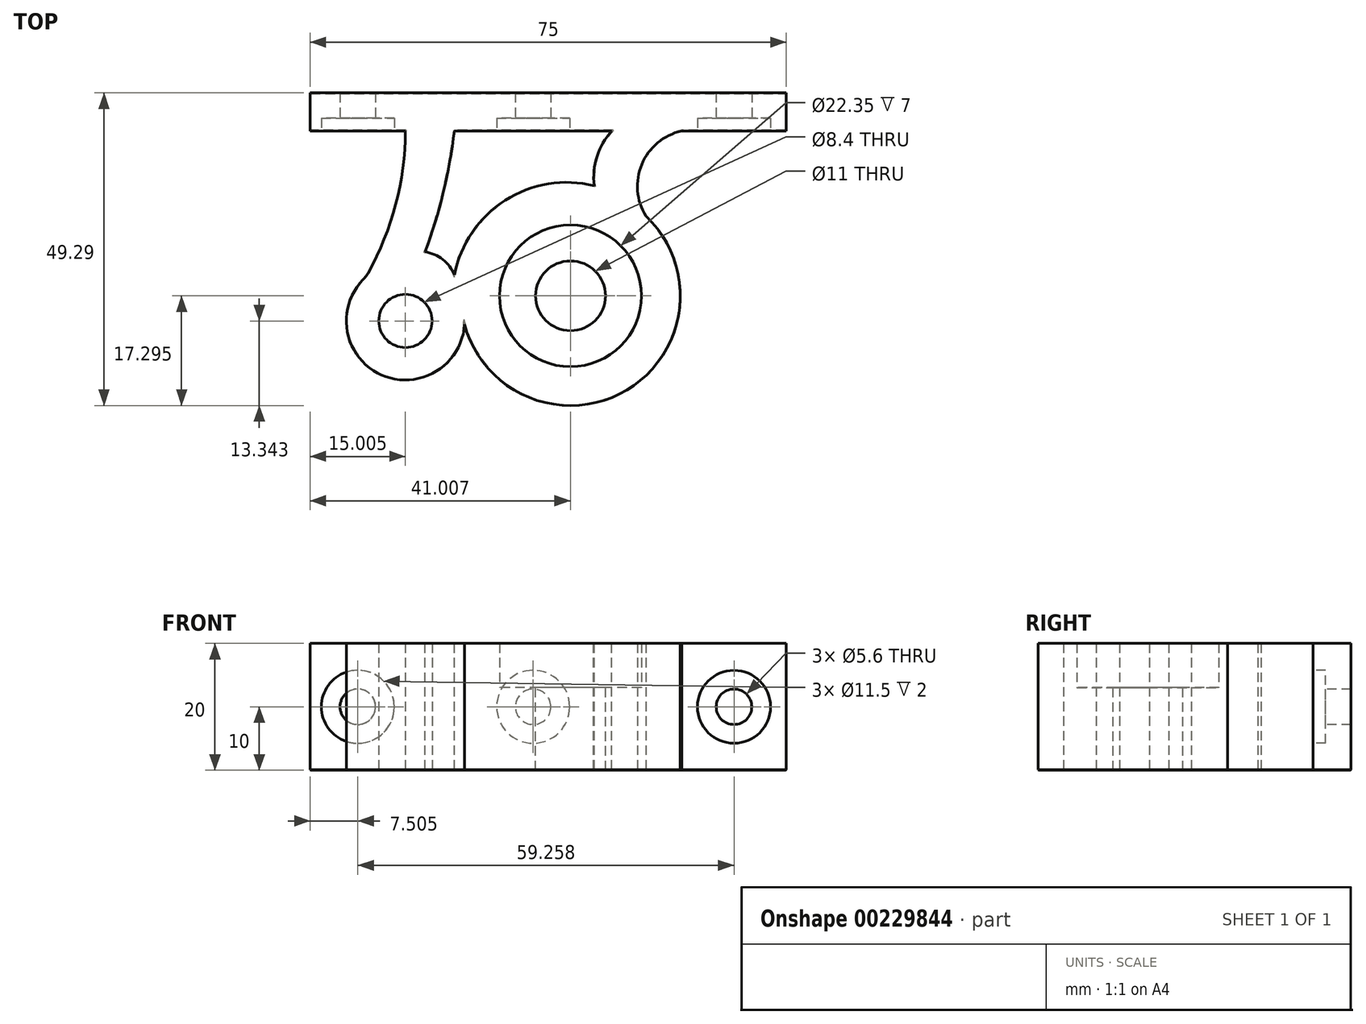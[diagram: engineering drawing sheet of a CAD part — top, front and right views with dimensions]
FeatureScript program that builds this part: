
annotation { "Feature Type Name" : "Feature", "Feature Type Description" : "" }
export const myFeature = defineFeature(function(context is Context, id is Id, definition is map)
    precondition{}
    {
        {
            var Q0;
            Q0=qCreatedBy(makeId("Top.planeOp"),FACE);
            var sketch = newSketch(context, id + "F0", { "sketchPlane" : qUnion([Q0])});
            skCircle(sketch, "E0", {"center": v(-26.48, -0.93) * mm, "radius": 4.2 * mm});
            skLineSegment(sketch, "E1", {"start": v(-26.48, -0.93) * mm, "end": v(-0.47, -0.93) * mm, "construction": true});
            skLineSegment(sketch, "E2", {"start": v(-0.47, -0.93) * mm, "end": v(-0.47, 3.02) * mm, "construction": true});
            skLineSegment(sketch, "E3", {"start": v(-26.48, -0.93) * mm, "end": v(-26.48, 35.02) * mm, "construction": true});
            skCircle(sketch, "E4", {"center": v(-0.47, 3.02) * mm, "radius": 11.18 * mm});
            skLineSegment(sketch, "E5", {"start": v(-26.48, 35.02) * mm, "end": v(-41.48, 35.02) * mm});
            skLineSegment(sketch, "E6", {"start": v(-41.48, 35.02) * mm, "end": v(-41.48, 29.02) * mm});
            skLineSegment(sketch, "E7", {"start": v(-26.48, 35.02) * mm, "end": v(33.52, 35.02) * mm});
            skLineSegment(sketch, "E8", {"start": v(33.52, 35.02) * mm, "end": v(33.52, 29.02) * mm});
            skLineSegment(sketch, "E9", {"start": v(17.04, 29.02) * mm, "end": v(33.52, 29.02) * mm});
            skLineSegment(sketch, "E10", {"start": v(-41.48, 29.02) * mm, "end": v(-26.48, 29.02) * mm});
            skArc(sketch, "E11", {"start": v(-32.73, 5.97) * mm, "mid": v(-30.5, -9.33) * mm, "end": v(-17.17, -1.48) * mm});
            skArc(sketch, "E12", {"start": v(-32.73, 5.97) * mm, "mid": v(-28.1, 17.09) * mm, "end": v(-26.48, 29.02) * mm});
            skArc(sketch, "E13", {"start": v(-17.17, -1.48) * mm, "mid": v(8.4, -11.83) * mm, "end": v(11.41, 15.6) * mm});
            skArc(sketch, "E14", {"start": v(17.04, 29.02) * mm, "mid": v(10.76, 23.76) * mm, "end": v(11.41, 15.6) * mm});
            skSolve(sketch);
        }
        {
            var Q0;
            Q0=makeQuery(id+"F0.imprint","IMPRINT",FACE,{"disambiguationData":[TD([[makeQuery(id+"F0.imprint","IMPRINT",EDGE,{"derivedFrom":sQuery(id+"F0.wireOp",EDGE,"E0")}),-1.0]])]});
            extrude(context, id + "F1", {"entities" : qUnion([Q0]), "depth" : 20 * mm});
        }
        {
            var Q0;
            Q0=makeQuery(id+"F1.opExtrude","CAP_FACE",FACE,{"disambiguationData":[OSD([sQuery(id+"F0.wireOp",EDGE,"E0"),sQuery(id+"F0.wireOp",EDGE,"E4"),sQuery(id+"F0.wireOp",EDGE,"E5"),sQuery(id+"F0.wireOp",EDGE,"E6"),sQuery(id+"F0.wireOp",EDGE,"E7"),sQuery(id+"F0.wireOp",EDGE,"E8"),sQuery(id+"F0.wireOp",EDGE,"rnpyxZyI-oq2V-pBoN-Qr8R-ykEtNN3jd1BS"),sQuery(id+"F0.wireOp",EDGE,"xY3NNHAz-ocZd-zQ1a-BtMq-btxev2WQv32X"),sQuery(id+"F0.wireOp",EDGE,"IQkoVCXJ-aQl7-kOCh-NkcK-sWtL1LuhfyMV"),sQuery(id+"F0.wireOp",EDGE,"E9"),sQuery(id+"F0.wireOp",EDGE,"E10"),sQuery(id+"F0.wireOp",EDGE,"rY0Ug5mX-zrsy-FKxN-pMBh-9Z9ctffI5Hmm"),sQuery(id+"F0.wireOp",EDGE,"HUhxcRyf-yDq1-n8Ah-xeCQ-rmbywmm5538G"),sQuery(id+"F0.wireOp",EDGE,"lBLZH0wx-sypd-l5w0-fRBg-AfOtDeXki2v4")])],"isStart":false});
            var sketch = newSketch(context, id + "F2", { "sketchPlane" : qUnion([Q0])});
            skLineSegment(sketch, "E15", {"start": v(-18.76, 29.02) * mm, "end": v(6.04, 29.02) * mm});
            skArc(sketch, "E16", {"start": v(-23.38, 9.94) * mm, "mid": v(-20.5, 19.35) * mm, "end": v(-18.76, 29.02) * mm});
            skArc(sketch, "E17", {"start": v(-18.76, 6.34) * mm, "mid": v(-20.58, 8.76) * mm, "end": v(-23.38, 9.94) * mm});
            skArc(sketch, "E18", {"start": v(3.26, 20.4) * mm, "mid": v(-10.76, 18.08) * mm, "end": v(-18.76, 6.34) * mm});
            skArc(sketch, "E19", {"start": v(6.04, 29.02) * mm, "mid": v(3.7, 25.02) * mm, "end": v(3.26, 20.4) * mm});
            skSolve(sketch);
        }
        {
            var Q0;
            Q0=makeQuery(id+"F2.imprint","IMPRINT",FACE,{"disambiguationData":[TD([[makeQuery(id+"F2.imprint","IMPRINT",EDGE,{"derivedFrom":sQuery(id+"F2.wireOp",EDGE,"E15")}),-1.0]])]});
            extrude(context, id + "F3", {"entities" : qUnion([Q0]), "operationType" : NewBodyOperationType.REMOVE, "oppositeDirection" : true, "depth" : 25 * mm});
        }
        {
            var Q0;
            Q0=makeQuery(id+"F1.opExtrude","SWEPT_FACE",FACE,{"disambiguationData":[OSD([sQuery(id+"F0.wireOp",EDGE,"E9")])]});
            var sketch = newSketch(context, id + "F4", { "sketchPlane" : qUnion([Q0])});
            skLineSegment(sketch, "E20", {"start": v(33.52, 10) * mm, "end": v(17.04, 10) * mm, "construction": true});
            skCircle(sketch, "E21", {"center": v(25.28, 10) * mm, "radius": 2.8 * mm});
            skSolve(sketch);
        }
        {
            var Q0;
            Q0=makeQuery(id+"F1.opExtrude","SWEPT_FACE",FACE,{"disambiguationData":[OSD([sQuery(id+"F0.wireOp",EDGE,"E10")])]});
            var sketch = newSketch(context, id + "F5", { "sketchPlane" : qUnion([Q0])});
            skLineSegment(sketch, "E22", {"start": v(-41.48, 10) * mm, "end": v(-26.48, 10) * mm, "construction": true});
            skCircle(sketch, "E23", {"center": v(-33.98, 10) * mm, "radius": 2.8 * mm});
            skSolve(sketch);
        }
        {
            var Q0;
            Q0=makeQuery(id+"F3.boolean.opBoolean","COPY",FACE,{"derivedFrom":makeQuery(id+"F3.opExtrude","SWEPT_FACE",FACE,{"disambiguationData":[OSD([sQuery(id+"F2.wireOp",EDGE,"E15")])]})});
            var sketch = newSketch(context, id + "F6", { "sketchPlane" : qUnion([Q0])});
            skLineSegment(sketch, "E24", {"start": v(-18.76, 10) * mm, "end": v(6.04, 10) * mm, "construction": true});
            skCircle(sketch, "E25", {"center": v(-6.36, 10) * mm, "radius": 2.8 * mm});
            skSolve(sketch);
        }
        {
            var Q0;
            Q0=makeQuery(id+"F4.imprint","IMPRINT",FACE,{"disambiguationData":[TD([[makeQuery(id+"F4.imprint","IMPRINT",EDGE,{"derivedFrom":sQuery(id+"F4.wireOp",EDGE,"E21")}),1.0]])]});
            var Q1;
            Q1=makeQuery(id+"F5.imprint","IMPRINT",FACE,{"disambiguationData":[TD([[makeQuery(id+"F5.imprint","IMPRINT",EDGE,{"derivedFrom":sQuery(id+"F5.wireOp",EDGE,"E23")}),1.0]])]});
            var Q2;
            Q2=makeQuery(id+"F6.imprint","IMPRINT",FACE,{"disambiguationData":[TD([[makeQuery(id+"F6.imprint","IMPRINT",EDGE,{"derivedFrom":sQuery(id+"F6.wireOp",EDGE,"E25")}),1.0]])]});
            extrude(context, id + "F7", {"entities" : qUnion([Q0, Q1, Q2]), "operationType" : NewBodyOperationType.REMOVE, "oppositeDirection" : true, "depth" : 25 * mm});
        }
        {
            var Q0;
            Q0=makeQuery(id+"F1.opExtrude","SWEPT_EDGE",EDGE,{"disambiguationData":[OSD([sQuery(id+"F0.wireOp",EDGE,"E11"),sQuery(id+"F0.wireOp",EDGE,"E12")])]});
            fillet(context, id + "F8", {"entities" : qUnion([Q0]), "radius" : 5 * mm, "tangentPropagation" : true, "allowEdgeOverflow" : false});
        }
        {
            var Q0;
            Q0=makeQuery(id+"F1.opExtrude","SWEPT_FACE",FACE,{"disambiguationData":[OSD([sQuery(id+"F0.wireOp",EDGE,"E10")])]});
            var sketch = newSketch(context, id + "F9", { "sketchPlane" : qUnion([Q0])});
            skCircle(sketch, "E26", {"center": v(-33.98, 10) * mm, "radius": 5.75 * mm});
            skSolve(sketch);
        }
        {
            var Q0;
            Q0=makeQuery(id+"F3.boolean.opBoolean","COPY",FACE,{"derivedFrom":makeQuery(id+"F3.opExtrude","SWEPT_FACE",FACE,{"disambiguationData":[OSD([sQuery(id+"F2.wireOp",EDGE,"E15")])]})});
            var sketch = newSketch(context, id + "F10", { "sketchPlane" : qUnion([Q0])});
            skCircle(sketch, "E27", {"center": v(-6.36, 10) * mm, "radius": 5.75 * mm});
            skSolve(sketch);
        }
        {
            var Q0;
            Q0=makeQuery(id+"F1.opExtrude","SWEPT_FACE",FACE,{"disambiguationData":[OSD([sQuery(id+"F0.wireOp",EDGE,"E9")])]});
            var sketch = newSketch(context, id + "F11", { "sketchPlane" : qUnion([Q0])});
            skCircle(sketch, "E28", {"center": v(25.28, 10) * mm, "radius": 5.75 * mm});
            skSolve(sketch);
        }
        {
            var Q0;
            Q0=makeQuery(id+"F9.imprint","IMPRINT",FACE,{"disambiguationData":[TD([[makeQuery(id+"F9.imprint","IMPRINT",EDGE,{"derivedFrom":sQuery(id+"F9.wireOp",EDGE,"E26")}),1.0]])]});
            var Q1;
            Q1=makeQuery(id+"F10.imprint","IMPRINT",FACE,{"disambiguationData":[TD([[makeQuery(id+"F10.imprint","IMPRINT",EDGE,{"derivedFrom":sQuery(id+"F10.wireOp",EDGE,"E27")}),1.0]])]});
            var Q2;
            Q2=makeQuery(id+"F11.imprint","IMPRINT",FACE,{"disambiguationData":[TD([[makeQuery(id+"F11.imprint","IMPRINT",EDGE,{"derivedFrom":sQuery(id+"F11.wireOp",EDGE,"E28")}),1.0]])]});
            extrude(context, id + "F12", {"entities" : qUnion([Q0, Q1, Q2]), "operationType" : NewBodyOperationType.REMOVE, "oppositeDirection" : true, "depth" : 2 * mm});
        }
        {
            var Q0;
            Q0=makeQuery(id+"F1.opExtrude","CAP_EDGE",EDGE,{"disambiguationData":[OSD([sQuery(id+"F0.wireOp",EDGE,"E5"),sQuery(id+"F0.wireOp",EDGE,"E7")])],"isStart":true});
            var Q1;
            Q1=makeQuery(id+"F1.opExtrude","CAP_EDGE",EDGE,{"disambiguationData":[OSD([sQuery(id+"F0.wireOp",EDGE,"E8")])],"isStart":true});
            var Q2;
            Q2=makeQuery(id+"F1.opExtrude","CAP_EDGE",EDGE,{"disambiguationData":[OSD([sQuery(id+"F0.wireOp",EDGE,"E9")])],"isStart":true});
            var Q3;
            Q3=makeQuery(id+"F3.boolean.opBoolean","INTERSECT",EDGE,{"derivedFrom":[makeQuery(id+"F1.opExtrude","CAP_FACE",FACE,{"disambiguationData":[OSD([sQuery(id+"F0.wireOp",EDGE,"E0"),sQuery(id+"F0.wireOp",EDGE,"E4"),sQuery(id+"F0.wireOp",EDGE,"E5"),sQuery(id+"F0.wireOp",EDGE,"E6"),sQuery(id+"F0.wireOp",EDGE,"E7"),sQuery(id+"F0.wireOp",EDGE,"E8"),sQuery(id+"F0.wireOp",EDGE,"E9"),sQuery(id+"F0.wireOp",EDGE,"E10"),sQuery(id+"F0.wireOp",EDGE,"E11"),sQuery(id+"F0.wireOp",EDGE,"E12"),sQuery(id+"F0.wireOp",EDGE,"E13"),sQuery(id+"F0.wireOp",EDGE,"E14")])],"isStart":true}),makeQuery(id+"F3.opExtrude","SWEPT_FACE",FACE,{"disambiguationData":[OSD([sQuery(id+"F2.wireOp",EDGE,"E15")])]})]});
            var Q4;
            Q4=makeQuery(id+"F1.opExtrude","CAP_EDGE",EDGE,{"disambiguationData":[OSD([sQuery(id+"F0.wireOp",EDGE,"E10")])],"isStart":true});
            var Q5;
            Q5=makeQuery(id+"F1.opExtrude","CAP_EDGE",EDGE,{"disambiguationData":[OSD([sQuery(id+"F0.wireOp",EDGE,"E6")])],"isStart":true});
            chamfer(context, id + "F13", {"entities" : qUnion([Q0, Q1, Q2, Q3, Q4, Q5]), "width" : .1 * mm, "tangentPropagation" : true});
        }
        {
            var Q0;
            Q0=makeQuery(id+"F1.opExtrude","CAP_EDGE",EDGE,{"disambiguationData":[OSD([sQuery(id+"F0.wireOp",EDGE,"E12")])],"isStart":true});
            var Q1;
            Q1=makeQuery(id+"F3.boolean.opBoolean","INTERSECT",EDGE,{"derivedFrom":[makeQuery(id+"F1.opExtrude","CAP_FACE",FACE,{"disambiguationData":[OSD([sQuery(id+"F0.wireOp",EDGE,"E0"),sQuery(id+"F0.wireOp",EDGE,"E4"),sQuery(id+"F0.wireOp",EDGE,"E5"),sQuery(id+"F0.wireOp",EDGE,"E6"),sQuery(id+"F0.wireOp",EDGE,"E7"),sQuery(id+"F0.wireOp",EDGE,"E8"),sQuery(id+"F0.wireOp",EDGE,"E9"),sQuery(id+"F0.wireOp",EDGE,"E10"),sQuery(id+"F0.wireOp",EDGE,"E11"),sQuery(id+"F0.wireOp",EDGE,"E12"),sQuery(id+"F0.wireOp",EDGE,"E13"),sQuery(id+"F0.wireOp",EDGE,"E14")])],"isStart":true}),makeQuery(id+"F3.opExtrude","SWEPT_FACE",FACE,{"disambiguationData":[OSD([sQuery(id+"F2.wireOp",EDGE,"E16")])]})]});
            var Q2;
            Q2=makeQuery(id+"F3.boolean.opBoolean","INTERSECT",EDGE,{"derivedFrom":[makeQuery(id+"F1.opExtrude","CAP_FACE",FACE,{"disambiguationData":[OSD([sQuery(id+"F0.wireOp",EDGE,"E0"),sQuery(id+"F0.wireOp",EDGE,"E4"),sQuery(id+"F0.wireOp",EDGE,"E5"),sQuery(id+"F0.wireOp",EDGE,"E6"),sQuery(id+"F0.wireOp",EDGE,"E7"),sQuery(id+"F0.wireOp",EDGE,"E8"),sQuery(id+"F0.wireOp",EDGE,"E9"),sQuery(id+"F0.wireOp",EDGE,"E10"),sQuery(id+"F0.wireOp",EDGE,"E11"),sQuery(id+"F0.wireOp",EDGE,"E12"),sQuery(id+"F0.wireOp",EDGE,"E13"),sQuery(id+"F0.wireOp",EDGE,"E14")])],"isStart":true}),makeQuery(id+"F3.opExtrude","SWEPT_FACE",FACE,{"disambiguationData":[OSD([sQuery(id+"F2.wireOp",EDGE,"E17")])]})]});
            var Q3;
            {var subQ0=sQuery(id+"F0.wireOp",EDGE,"E12");var subQ1=sQuery(id+"F0.wireOp",EDGE,"E11");Q3=makeQuery(id+"F8.opFillet","BLEND_EDGE",EDGE,{"blendedFrom":[makeQuery(id+"F1.opExtrude","SWEPT_EDGE",EDGE,{"disambiguationData":[OSD([subQ1,subQ0])]}),makeQuery(id+"F1.opExtrude","CAP_FACE",FACE,{"disambiguationData":[OSD([sQuery(id+"F0.wireOp",EDGE,"E0"),sQuery(id+"F0.wireOp",EDGE,"E4"),sQuery(id+"F0.wireOp",EDGE,"E5"),sQuery(id+"F0.wireOp",EDGE,"E6"),sQuery(id+"F0.wireOp",EDGE,"E7"),sQuery(id+"F0.wireOp",EDGE,"E8"),sQuery(id+"F0.wireOp",EDGE,"E9"),sQuery(id+"F0.wireOp",EDGE,"E10"),subQ1,subQ0,sQuery(id+"F0.wireOp",EDGE,"E13"),sQuery(id+"F0.wireOp",EDGE,"E14")])],"isStart":true})],"blendedInto":[makeQuery(id+"F1.opExtrude","CAP_FACE",FACE,{"disambiguationData":[OSD([sQuery(id+"F0.wireOp",EDGE,"E0"),sQuery(id+"F0.wireOp",EDGE,"E4"),sQuery(id+"F0.wireOp",EDGE,"E5"),sQuery(id+"F0.wireOp",EDGE,"E6"),sQuery(id+"F0.wireOp",EDGE,"E7"),sQuery(id+"F0.wireOp",EDGE,"E8"),sQuery(id+"F0.wireOp",EDGE,"E9"),sQuery(id+"F0.wireOp",EDGE,"E10"),subQ1,subQ0,sQuery(id+"F0.wireOp",EDGE,"E13"),sQuery(id+"F0.wireOp",EDGE,"E14")])],"isStart":true})]});}
            var Q4;
            Q4=makeQuery(id+"F1.opExtrude","CAP_EDGE",EDGE,{"disambiguationData":[OSD([sQuery(id+"F0.wireOp",EDGE,"E13")])],"isStart":true});
            var Q5;
            Q5=makeQuery(id+"F3.boolean.opBoolean","INTERSECT",EDGE,{"derivedFrom":[makeQuery(id+"F1.opExtrude","CAP_FACE",FACE,{"disambiguationData":[OSD([sQuery(id+"F0.wireOp",EDGE,"E0"),sQuery(id+"F0.wireOp",EDGE,"E4"),sQuery(id+"F0.wireOp",EDGE,"E5"),sQuery(id+"F0.wireOp",EDGE,"E6"),sQuery(id+"F0.wireOp",EDGE,"E7"),sQuery(id+"F0.wireOp",EDGE,"E8"),sQuery(id+"F0.wireOp",EDGE,"E9"),sQuery(id+"F0.wireOp",EDGE,"E10"),sQuery(id+"F0.wireOp",EDGE,"E11"),sQuery(id+"F0.wireOp",EDGE,"E12"),sQuery(id+"F0.wireOp",EDGE,"E13"),sQuery(id+"F0.wireOp",EDGE,"E14")])],"isStart":true}),makeQuery(id+"F3.opExtrude","SWEPT_FACE",FACE,{"disambiguationData":[OSD([sQuery(id+"F2.wireOp",EDGE,"E18")])]})]});
            var Q6;
            Q6=makeQuery(id+"F1.opExtrude","CAP_EDGE",EDGE,{"disambiguationData":[OSD([sQuery(id+"F0.wireOp",EDGE,"E14")])],"isStart":true});
            var Q7;
            Q7=makeQuery(id+"F3.boolean.opBoolean","INTERSECT",EDGE,{"derivedFrom":[makeQuery(id+"F1.opExtrude","CAP_FACE",FACE,{"disambiguationData":[OSD([sQuery(id+"F0.wireOp",EDGE,"E0"),sQuery(id+"F0.wireOp",EDGE,"E4"),sQuery(id+"F0.wireOp",EDGE,"E5"),sQuery(id+"F0.wireOp",EDGE,"E6"),sQuery(id+"F0.wireOp",EDGE,"E7"),sQuery(id+"F0.wireOp",EDGE,"E8"),sQuery(id+"F0.wireOp",EDGE,"E9"),sQuery(id+"F0.wireOp",EDGE,"E10"),sQuery(id+"F0.wireOp",EDGE,"E11"),sQuery(id+"F0.wireOp",EDGE,"E12"),sQuery(id+"F0.wireOp",EDGE,"E13"),sQuery(id+"F0.wireOp",EDGE,"E14")])],"isStart":true}),makeQuery(id+"F3.opExtrude","SWEPT_FACE",FACE,{"disambiguationData":[OSD([sQuery(id+"F2.wireOp",EDGE,"E19")])]})]});
            chamfer(context, id + "F14", {"entities" : qUnion([Q0, Q1, Q2, Q3, Q4, Q5, Q6, Q7]), "width" : .1 * mm, "tangentPropagation" : true});
        }
        {
            var Q0;
            Q0=makeQuery(id+"F1.opExtrude","CAP_FACE",FACE,{"disambiguationData":[OSD([sQuery(id+"F0.wireOp",EDGE,"E0"),sQuery(id+"F0.wireOp",EDGE,"E4"),sQuery(id+"F0.wireOp",EDGE,"E5"),sQuery(id+"F0.wireOp",EDGE,"E6"),sQuery(id+"F0.wireOp",EDGE,"E7"),sQuery(id+"F0.wireOp",EDGE,"E8"),sQuery(id+"F0.wireOp",EDGE,"E9"),sQuery(id+"F0.wireOp",EDGE,"E10"),sQuery(id+"F0.wireOp",EDGE,"E11"),sQuery(id+"F0.wireOp",EDGE,"E12"),sQuery(id+"F0.wireOp",EDGE,"E13"),sQuery(id+"F0.wireOp",EDGE,"E14")])],"isStart":true});
            var sketch = newSketch(context, id + "F15", { "sketchPlane" : qUnion([Q0])});
            skCircle(sketch, "E29", {"center": v(-0.47, -3.02) * mm, "radius": 12.1 * mm});
            skSolve(sketch);
        }
        {
            var Q0;
            Q0=makeQuery(id+"F15.imprint","IMPRINT",FACE,{"disambiguationData":[TD([[makeQuery(id+"F15.imprint","IMPRINT",EDGE,{"derivedFrom":makeQuery(id+"F1.opExtrude","CAP_EDGE",EDGE,{"disambiguationData":[OSD([sQuery(id+"F0.wireOp",EDGE,"E4")])],"isStart":true})}),-1.0]])]});
            extrude(context, id + "F16", {"entities" : qUnion([Q0]), "operationType" : NewBodyOperationType.ADD, "oppositeDirection" : true, "depth" : 13 * mm});
        }
        {
            var Q0;
            Q0=makeQuery(id+"F16.opExtrude","CAP_FACE",FACE,{"disambiguationData":[OSD([sQuery(id+"F0.wireOp",EDGE,"E4")])],"isStart":false});
            var sketch = newSketch(context, id + "F17", { "sketchPlane" : qUnion([Q0])});
            skCircle(sketch, "E30", {"center": v(-0.47, 3.02) * mm, "radius": 5.5 * mm});
            skSolve(sketch);
        }
        {
            var Q0;
            Q0=makeQuery(id+"F17.imprint","IMPRINT",FACE,{"disambiguationData":[TD([[makeQuery(id+"F17.imprint","IMPRINT",EDGE,{"derivedFrom":sQuery(id+"F17.wireOp",EDGE,"E30")}),1.0]])]});
            extrude(context, id + "F18", {"entities" : qUnion([Q0]), "operationType" : NewBodyOperationType.REMOVE, "oppositeDirection" : true, "depth" : 25 * mm});
        }
    });
